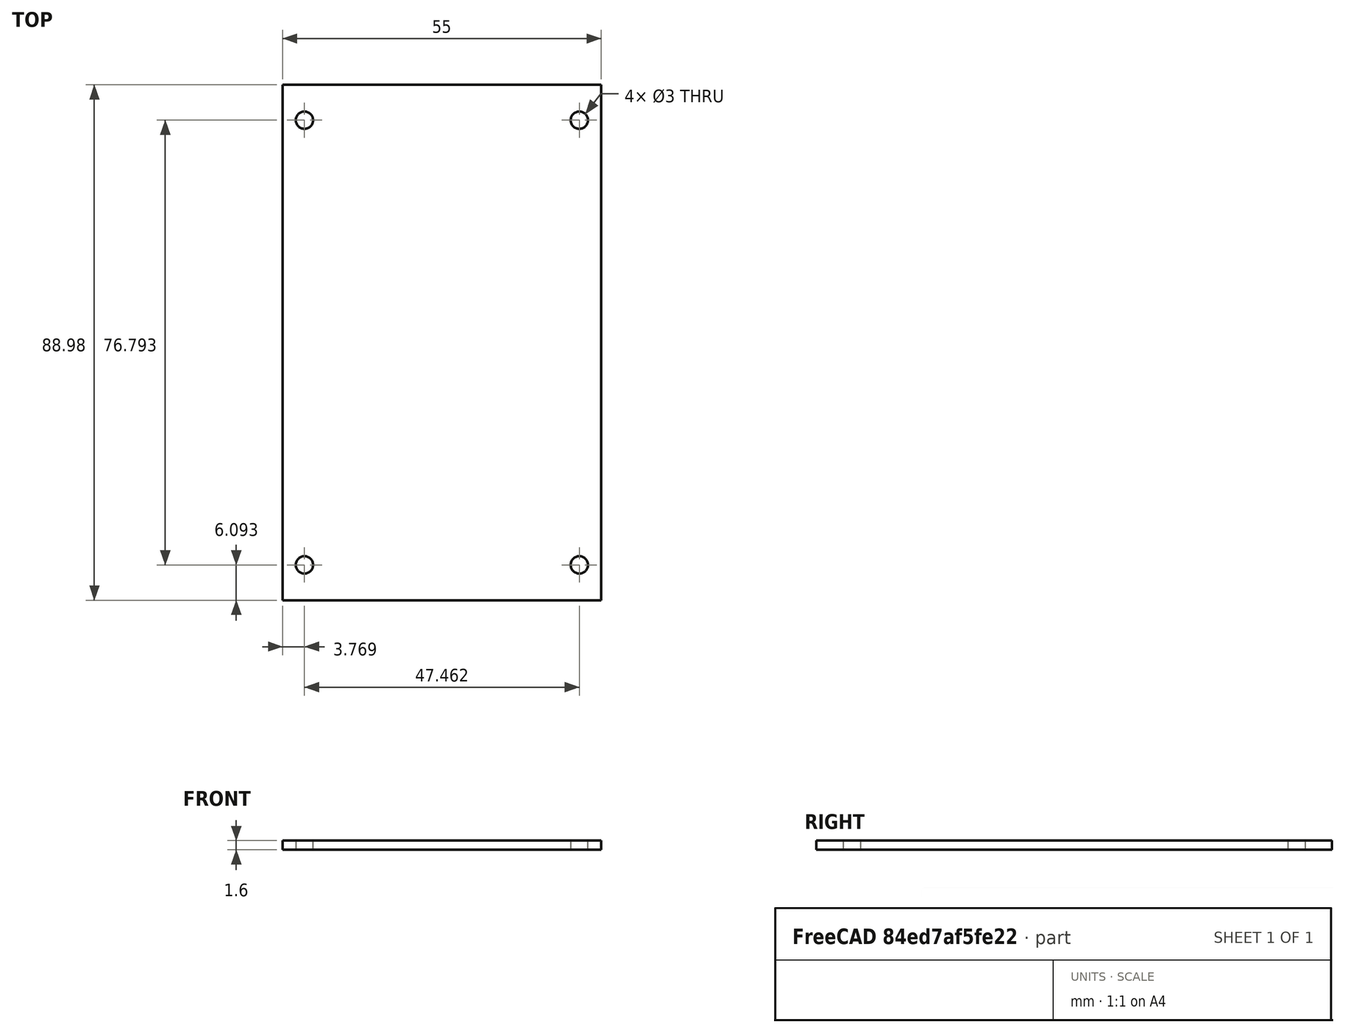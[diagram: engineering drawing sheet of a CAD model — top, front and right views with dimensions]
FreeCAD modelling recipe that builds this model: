
FCSTD DOCUMENT  (FreeCAD 0.17R13541 (Git))
Label: PCB
License: All rights reserved
LicenseURL: http://en.wikipedia.org/wiki/All_rights_reserved
objects: Spreadsheet::Sheet×1, Sketcher::SketchObject×1, Part::Extrusion×1
note: 2 computed .brp shape members not serialized (recipe doc carries the construction recipe); baked Part::Feature solids carry a one-line shape summary decoded from their .brp

FEATURE [Spreadsheet::Sheet] Spreadsheet
  cells = A1=PCB Width; B1(PCB_Width)==55mm; A2=PCB Length; B2(PCB_Length)==B1 * 1.6180000000000001
FEATURE [Sketcher::SketchObject] Sketch
  expr: Constraints[17] = Spreadsheet.PCB_Length
  expr: Constraints[16] = Spreadsheet.PCB_Width
  sketch-geometry (11):
    g0: LineSegment StartX=-27.5 StartY=44.495 StartZ=0 EndX=27.5 EndY=44.495 EndZ=0
    g1: LineSegment StartX=27.5 StartY=44.495 StartZ=0 EndX=27.5 EndY=-44.495 EndZ=0
    g2: LineSegment StartX=27.5 StartY=-44.495 StartZ=0 EndX=-27.5 EndY=-44.495 EndZ=0
    g3: LineSegment StartX=-27.5 StartY=-44.495 StartZ=0 EndX=-27.5 EndY=44.495 EndZ=0
    g4: LineSegment [constr] StartX=-27.5 StartY=44.495 StartZ=0 EndX=0 EndY=0 EndZ=0
    g5: LineSegment [constr] StartX=27.5 StartY=-44.495 StartZ=0 EndX=0 EndY=0 EndZ=0
    g6: LineSegment [constr] StartX=-27.5 StartY=-44.495 StartZ=0 EndX=27.5 EndY=44.495 EndZ=0
    g7: Circle CenterX=-23.731 CenterY=38.3967 CenterZ=0 NormalX=0 NormalY=0 NormalZ=1 AngleXU=0 Radius=1.5
    g8: Circle CenterX=23.731 CenterY=38.3967 CenterZ=0 NormalX=0 NormalY=0 NormalZ=1 AngleXU=0 Radius=1.5
    g9: Circle CenterX=-23.731 CenterY=-38.3967 CenterZ=0 NormalX=0 NormalY=0 NormalZ=1 AngleXU=0 Radius=1.5
    g10: Circle CenterX=23.731 CenterY=-38.3967 CenterZ=0 NormalX=0 NormalY=0 NormalZ=1 AngleXU=0 Radius=1.5
  constraints (30):
    c: Coincident(g0,g1)
    c: Coincident(g1,g2)
    c: Coincident(g2,g3)
    c: Coincident(g3,g0)
    c: Horizontal(g0)
    c: Horizontal(g2)
    c: Vertical(g1)
    c: Vertical(g3)
    c: Coincident(g4,g0)
    c: Coincident(g4,g-1)
    c: Coincident(g5,g1)
    c: Coincident(g5,g-1)
    c: Coincident(g6,g2)
    c: Coincident(g6,g0)
    c: Parallel(g4,g5)
    c: Equal(g4,g5)
    c: Distance(g0) = 55
    c: Distance(g1) = 88.99
    c: PointOnObject(g7,g4)
    c: PointOnObject(g8,g6)
    c: PointOnObject(g10,g5)
    c: Equal(g9,g7)
    c: Equal(g8,g10)
    c: Equal(g10,g9)
    c: Radius(g7) = 1.5
    c: Horizontal(g7,g8)
    c: Vertical(g7,g9)
    c: Vertical(g10,g8)
    c: PointOnObject(g9,g6)
    c: Distance(g7,g0) = 7.16897
FEATURE [Part::Extrusion] Extrude
  Base = -> Sketch
  Dir = (0,0,1)
  DirMode = 2
  FaceMakerClass = Part::FaceMakerBullseye
  LengthFwd = 1.6
  LengthRev = 0
  Solid = true
  Symmetric = false
